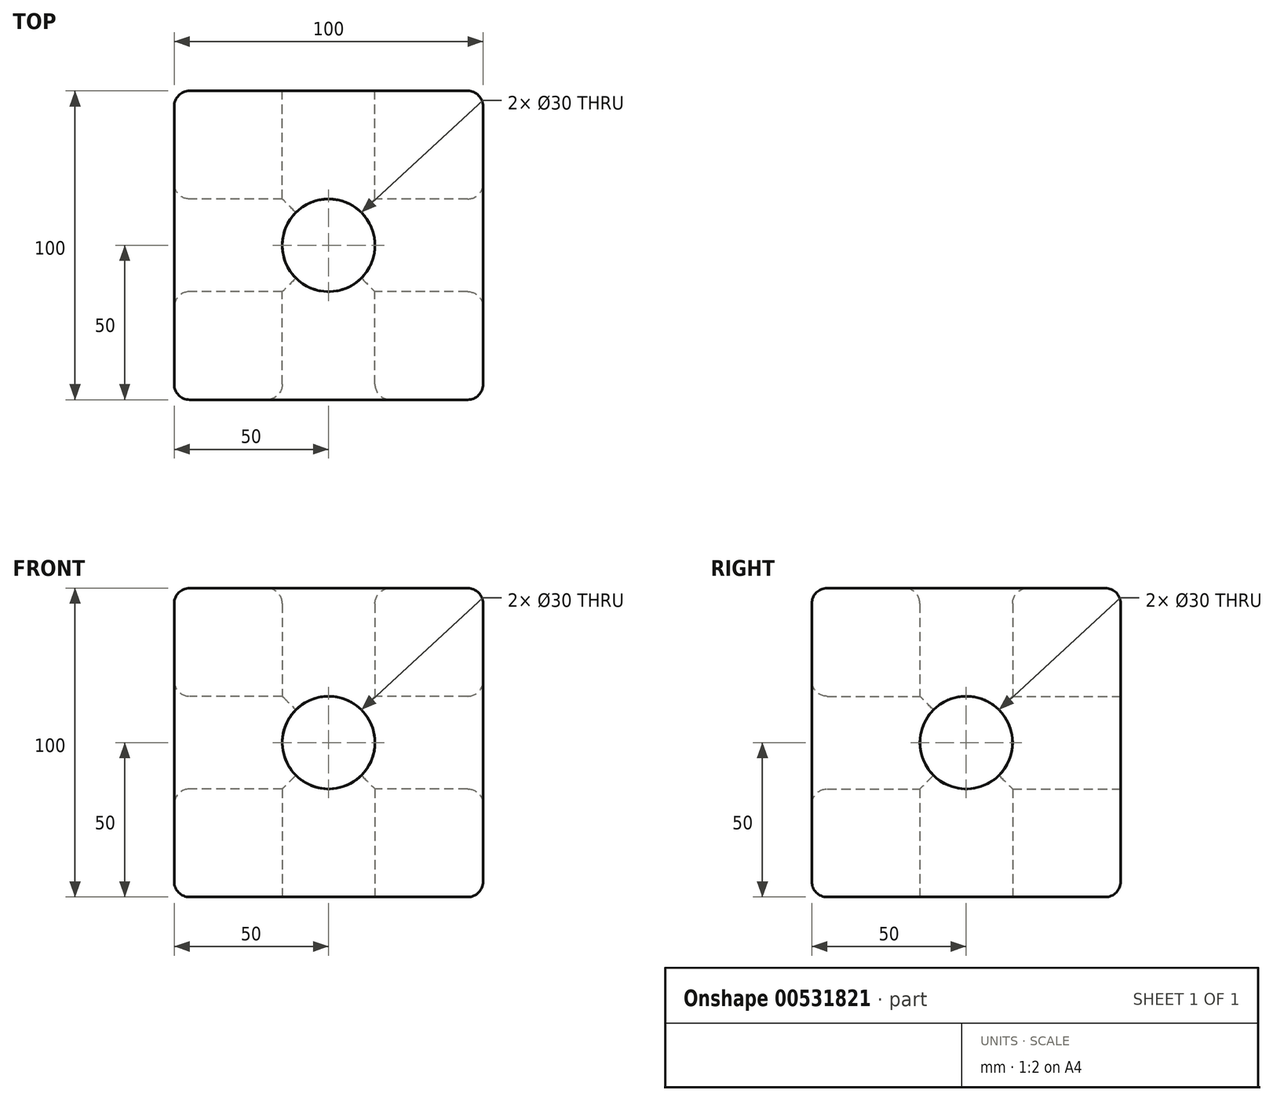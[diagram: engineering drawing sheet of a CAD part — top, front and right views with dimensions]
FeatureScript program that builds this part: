
annotation { "Feature Type Name" : "Feature", "Feature Type Description" : "" }
export const myFeature = defineFeature(function(context is Context, id is Id, definition is map)
    precondition{}
    {
        {
            var Q0;
            Q0=qCreatedBy(makeId("Front.planeOp"),FACE);
            var sketch = newSketch(context, id + "F0", { "sketchPlane" : qUnion([Q0])});
            skLineSegment(sketch, "E0.bottom", {"start": v(50, -50) * mm, "end": v(-50, -50) * mm});
            skLineSegment(sketch, "E0.top", {"start": v(50, 50) * mm, "end": v(-50, 50) * mm});
            skLineSegment(sketch, "E0.left", {"start": v(50, -50) * mm, "end": v(50, 50) * mm});
            skLineSegment(sketch, "E0.right", {"start": v(-50, -50) * mm, "end": v(-50, 50) * mm});
            skPoint(sketch, "E0.middle", {"position": v(0, 0) * mm});
            skSolve(sketch);
        }
        {
            var Q0;
            Q0 = qSketchRegion(id + "F0", true);
            extrude(context, id + "F1", {"entities" : qUnion([Q0]), "depth" : 100 * mm, "offsetDistance" : 25 * mm});
        }
        {
            var Q0;
            Q0=makeQuery(id+"F1.opExtrude","SWEPT_FACE",FACE,{"disambiguationData":[OSD([sQuery(id+"F0.wireOp",EDGE,"E0.right")])]});
            var sketch = newSketch(context, id + "F2", { "sketchPlane" : qUnion([Q0])});
            skCircle(sketch, "E1", {"center": v(50, 0) * mm, "radius": 15 * mm});
            skSolve(sketch);
        }
        {
            var Q0;
            Q0 = qSketchRegion(id + "F2", true);
            extrude(context, id + "F3", {"entities" : qUnion([Q0]), "operationType" : NewBodyOperationType.REMOVE, "endBound" : BoundingType.THROUGH_ALL, "oppositeDirection" : true, "depth" : 25 * mm, "offsetDistance" : 25 * mm});
        }
        {
            var Q0;
            Q0=makeQuery(id+"F1.opExtrude","CAP_FACE",FACE,{"disambiguationData":[OSD([sQuery(id+"F0.wireOp",EDGE,"E0.bottom"),sQuery(id+"F0.wireOp",EDGE,"E0.top"),sQuery(id+"F0.wireOp",EDGE,"E0.left"),sQuery(id+"F0.wireOp",EDGE,"E0.right")])],"isStart":true});
            var sketch = newSketch(context, id + "F4", { "sketchPlane" : qUnion([Q0])});
            skCircle(sketch, "E2", {"center": v(0, 0) * mm, "radius": 15 * mm});
            skSolve(sketch);
        }
        {
            var Q0;
            Q0 = qSketchRegion(id + "F4", true);
            extrude(context, id + "F5", {"entities" : qUnion([Q0]), "operationType" : NewBodyOperationType.REMOVE, "endBound" : BoundingType.THROUGH_ALL, "oppositeDirection" : true, "depth" : 25 * mm, "offsetDistance" : 25 * mm});
        }
        {
            var Q0;
            Q0=makeQuery(id+"F1.opExtrude","SWEPT_FACE",FACE,{"disambiguationData":[OSD([sQuery(id+"F0.wireOp",EDGE,"E0.bottom")])]});
            var sketch = newSketch(context, id + "F6", { "sketchPlane" : qUnion([Q0])});
            skCircle(sketch, "E3", {"center": v(0, 50) * mm, "radius": 15 * mm});
            skSolve(sketch);
        }
        {
            var Q0;
            Q0 = qSketchRegion(id + "F6", true);
            extrude(context, id + "F7", {"entities" : qUnion([Q0]), "operationType" : NewBodyOperationType.REMOVE, "endBound" : BoundingType.THROUGH_ALL, "oppositeDirection" : true, "depth" : 25 * mm, "offsetDistance" : 25 * mm});
        }
        {
            var Q0;
            Q0=makeQuery(id+"F1.opExtrude","CAP_EDGE",EDGE,{"disambiguationData":[OSD([sQuery(id+"F0.wireOp",EDGE,"E0.top")])],"isStart":true});
            var Q1;
            Q1=makeQuery(id+"F1.opExtrude","SWEPT_EDGE",EDGE,{"disambiguationData":[OSD([sQuery(id+"F0.wireOp",EDGE,"E0.top"),sQuery(id+"F0.wireOp",EDGE,"E0.right")])]});
            var Q2;
            Q2=makeQuery(id+"F1.opExtrude","CAP_EDGE",EDGE,{"disambiguationData":[OSD([sQuery(id+"F0.wireOp",EDGE,"E0.right")])],"isStart":true});
            var Q3;
            Q3=makeQuery(id+"F1.opExtrude","SWEPT_EDGE",EDGE,{"disambiguationData":[OSD([sQuery(id+"F0.wireOp",EDGE,"E0.bottom"),sQuery(id+"F0.wireOp",EDGE,"E0.right")])]});
            var Q4;
            Q4=makeQuery(id+"F1.opExtrude","CAP_EDGE",EDGE,{"disambiguationData":[OSD([sQuery(id+"F0.wireOp",EDGE,"E0.bottom")])],"isStart":true});
            var Q5;
            Q5=makeQuery(id+"F1.opExtrude","CAP_EDGE",EDGE,{"disambiguationData":[OSD([sQuery(id+"F0.wireOp",EDGE,"E0.left")])],"isStart":true});
            var Q6;
            Q6=makeQuery(id+"F1.opExtrude","SWEPT_FACE",FACE,{"disambiguationData":[OSD([sQuery(id+"F0.wireOp",EDGE,"E0.right")])]});
            var Q7;
            Q7=makeQuery(id+"F1.opExtrude","CAP_EDGE",EDGE,{"disambiguationData":[OSD([sQuery(id+"F0.wireOp",EDGE,"E0.bottom")])],"isStart":false});
            var Q8;
            Q8=makeQuery(id+"F1.opExtrude","SWEPT_EDGE",EDGE,{"disambiguationData":[OSD([sQuery(id+"F0.wireOp",EDGE,"E0.bottom"),sQuery(id+"F0.wireOp",EDGE,"E0.left")])]});
            var Q9;
            Q9=makeQuery(id+"F1.opExtrude","SWEPT_EDGE",EDGE,{"disambiguationData":[OSD([sQuery(id+"F0.wireOp",EDGE,"E0.top"),sQuery(id+"F0.wireOp",EDGE,"E0.left")])]});
            var Q10;
            Q10=makeQuery(id+"F1.opExtrude","CAP_EDGE",EDGE,{"disambiguationData":[OSD([sQuery(id+"F0.wireOp",EDGE,"E0.left")])],"isStart":false});
            var Q11;
            Q11=makeQuery(id+"F1.opExtrude","CAP_EDGE",EDGE,{"disambiguationData":[OSD([sQuery(id+"F0.wireOp",EDGE,"E0.top")])],"isStart":false});
            fillet(context, id + "F8", {"entities" : qUnion([Q0, Q1, Q2, Q3, Q4, Q5, Q6, Q7, Q8, Q9, Q10, Q11]), "radius" : 5 * mm, "tangentPropagation" : true, "allowEdgeOverflow" : false});
        }
        {
            var Q0;
            Q0=makeQuery(id+"F7.boolean.opBoolean","INTERSECT",EDGE,{"derivedFrom":[makeQuery(id+"F1.opExtrude","SWEPT_FACE",FACE,{"disambiguationData":[OSD([sQuery(id+"F0.wireOp",EDGE,"E0.top")])]}),makeQuery(id+"F7.opExtrude","SWEPT_FACE",FACE,{"disambiguationData":[OSD([sQuery(id+"F6.wireOp",EDGE,"E3")])]})]});
            var Q1;
            Q1=makeQuery(id+"F5.boolean.opBoolean","INTERSECT",EDGE,{"derivedFrom":[makeQuery(id+"F1.opExtrude","CAP_FACE",FACE,{"disambiguationData":[OSD([sQuery(id+"F0.wireOp",EDGE,"E0.bottom"),sQuery(id+"F0.wireOp",EDGE,"E0.top"),sQuery(id+"F0.wireOp",EDGE,"E0.left"),sQuery(id+"F0.wireOp",EDGE,"E0.right")])],"isStart":false}),makeQuery(id+"F5.opExtrude","SWEPT_FACE",FACE,{"disambiguationData":[OSD([sQuery(id+"F4.wireOp",EDGE,"E2")])]})]});
            var Q2;
            Q2=makeQuery(id+"F3.boolean.opBoolean","INTERSECT",EDGE,{"derivedFrom":[makeQuery(id+"F1.opExtrude","SWEPT_FACE",FACE,{"disambiguationData":[OSD([sQuery(id+"F0.wireOp",EDGE,"E0.left")])]}),makeQuery(id+"F3.opExtrude","SWEPT_FACE",FACE,{"disambiguationData":[OSD([sQuery(id+"F2.wireOp",EDGE,"E1")])]})]});
            var Q3;
            Q3=makeQuery(id+"F5.boolean.opBoolean","COPY",EDGE,{"derivedFrom":makeQuery(id+"F5.opExtrude","CAP_EDGE",EDGE,{"disambiguationData":[OSD([sQuery(id+"F4.wireOp",EDGE,"E2")])],"isStart":true})});
            var Q4;
            Q4=makeQuery(id+"F7.boolean.opBoolean","COPY",EDGE,{"derivedFrom":makeQuery(id+"F7.opExtrude","CAP_EDGE",EDGE,{"disambiguationData":[OSD([sQuery(id+"F6.wireOp",EDGE,"E3")])],"isStart":true})});
            fillet(context, id + "F9", {"entities" : qUnion([Q0, Q1, Q2, Q3, Q4]), "radius" : 5 * mm, "tangentPropagation" : true, "allowEdgeOverflow" : false});
        }
    });
